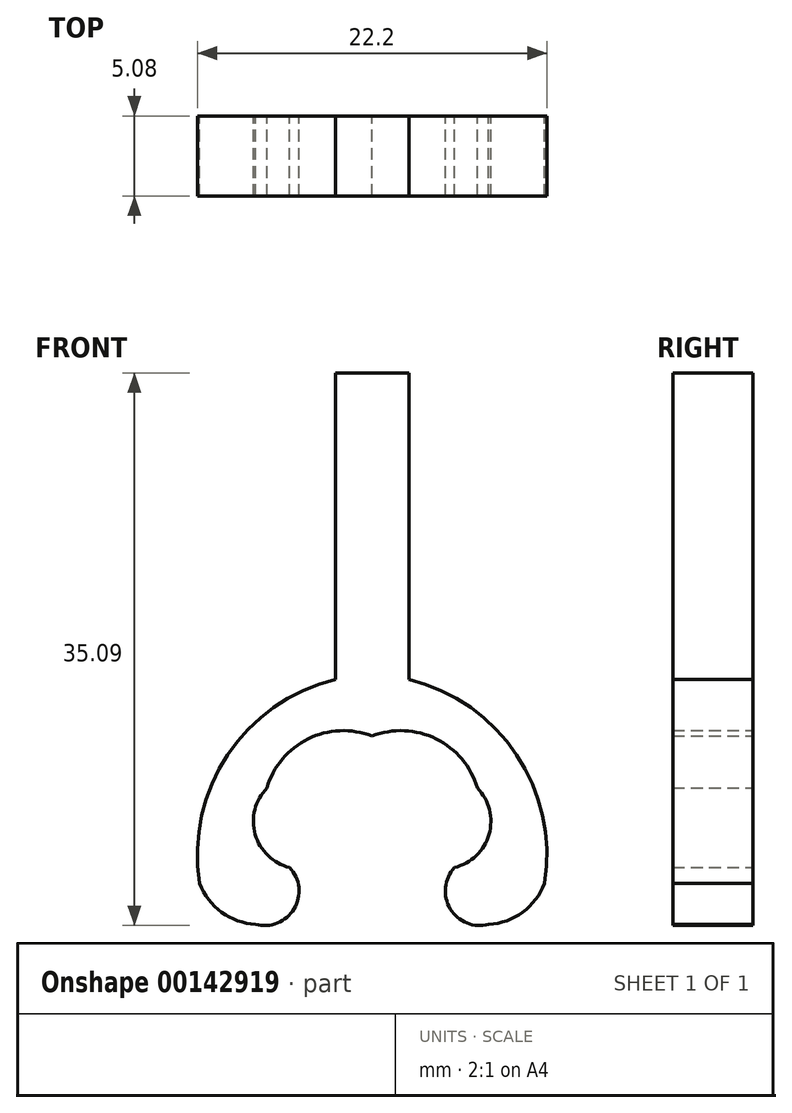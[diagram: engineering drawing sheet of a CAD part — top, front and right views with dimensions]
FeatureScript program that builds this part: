
annotation { "Feature Type Name" : "Feature", "Feature Type Description" : "" }
export const myFeature = defineFeature(function(context is Context, id is Id, definition is map)
    precondition{}
    {
        {
            var Q0;
            Q0=qCreatedBy(makeId("Front.planeOp"),FACE);
            var sketch = newSketch(context, id + "F0", { "sketchPlane" : qUnion([Q0])});
            skLineSegment(sketch, "E0", {"start": v(-2.33, 0) * mm, "end": v(-2.33, 19.47) * mm});
            skLineSegment(sketch, "E1", {"start": v(-2.33, 19.47) * mm, "end": v(0, 19.47) * mm});
            skArc(sketch, "E2", {"start": v(-2.33, 0) * mm, "mid": v(-9.18, -4.78) * mm, "end": v(-10.95, -12.95) * mm});
            skArc(sketch, "E3", {"start": v(-10.95, -12.95) * mm, "mid": v(-9.56, -14.78) * mm, "end": v(-7.4, -15.54) * mm});
            skArc(sketch, "E4", {"start": v(-7.4, -15.54) * mm, "mid": v(-4.96, -14.56) * mm, "end": v(-5.24, -11.94) * mm});
            skArc(sketch, "E5", {"start": v(-6.68, -6.89) * mm, "mid": v(-7.42, -9.83) * mm, "end": v(-5.24, -11.94) * mm});
            skArc(sketch, "E6", {"start": v(0, -3.59) * mm, "mid": v(-4.07, -3.76) * mm, "end": v(-6.68, -6.89) * mm});
            skLineSegment(sketch, "E7", {"start": v(0, 21.97) * mm, "end": v(0, -15.24) * mm, "construction": true});
            skLineSegment(sketch, "E8.MirrorCS", {"start": v(2.33, 0) * mm, "end": v(2.33, 19.47) * mm});
            skLineSegment(sketch, "E9.MirrorCS", {"start": v(2.33, 19.47) * mm, "end": v(0, 19.47) * mm});
            skArc(sketch, "E10.MirrorCS", {"start": v(2.33, 0) * mm, "mid": v(9.18, -4.78) * mm, "end": v(10.95, -12.95) * mm});
            skArc(sketch, "E11.MirrorCS", {"start": v(0, -3.59) * mm, "mid": v(4.07, -3.76) * mm, "end": v(6.68, -6.89) * mm});
            skArc(sketch, "E12.MirrorCS", {"start": v(10.95, -12.95) * mm, "mid": v(9.56, -14.78) * mm, "end": v(7.4, -15.54) * mm});
            skArc(sketch, "E13.MirrorCS", {"start": v(7.4, -15.54) * mm, "mid": v(4.96, -14.56) * mm, "end": v(5.24, -11.94) * mm});
            skArc(sketch, "E14.MirrorCS", {"start": v(6.68, -6.89) * mm, "mid": v(7.42, -9.83) * mm, "end": v(5.24, -11.94) * mm});
            skSolve(sketch);
        }
        {
            var Q0;
            Q0=makeQuery(id+"F0.imprint","IMPRINT",FACE,{"disambiguationData":[TD([[makeQuery(id+"F0.imprint","IMPRINT",EDGE,{"derivedFrom":sQuery(id+"F0.wireOp",EDGE,"E0")}),-1.0]])]});
            extrude(context, id + "F1", {"entities" : qUnion([Q0]), "depth" : 5.08 * mm});
        }
    });
